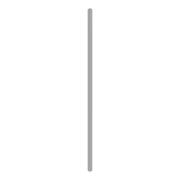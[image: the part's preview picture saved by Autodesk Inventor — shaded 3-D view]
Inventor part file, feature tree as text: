
AUTODESK INVENTOR PART (.ipt)
format: ipt  version: 2020.3 (Build 243373000, 373)  size: 89,600 bytes
history: native  units: mm
features: other x1, extrude x1, sketch x1
ambient origin geometry x8: Origin, YZ Plane, XZ Plane, XY Plane, X Axis, Y Axis, Z Axis, Center Point
bodies: Body1 (feature_tree)
feature tree (3):
  other  "Sólido1"
  extrude  "Extrusão1"  Depth=40.0mm
  sketch  "Esboço1"  dims[d0=40.0mm d1=40.0mm d2=1.5mm d3=1.5mm d4=2500.0mm d5=0.0mm]
